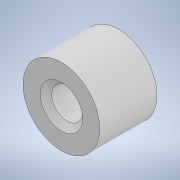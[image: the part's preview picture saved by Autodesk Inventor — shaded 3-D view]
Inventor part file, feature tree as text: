
AUTODESK INVENTOR PART (.ipt)
format: ipt  version: 2020 (Build 240168000, 168)  size: 104,448 bytes
history: native  units: mm
features: extrude x1, chamfer x1, sketch x1
ambient origin geometry x8: Origin, YZ Plane, XZ Plane, XY Plane, X Axis, Y Axis, Z Axis, Center Point
bodies: Solid1 (feature_tree)
feature tree (3):
  extrude  "Extrusion1"  Depth=5.0mm
  chamfer  "Chamfer1"  Distance=5.0mm
  sketch  "Sketch1"  dims[d0=2.7mm d1=2.0mm d2=5.0mm d3=0.0mm d4=0.5mm d5=2.0mm d6=45.0deg]
